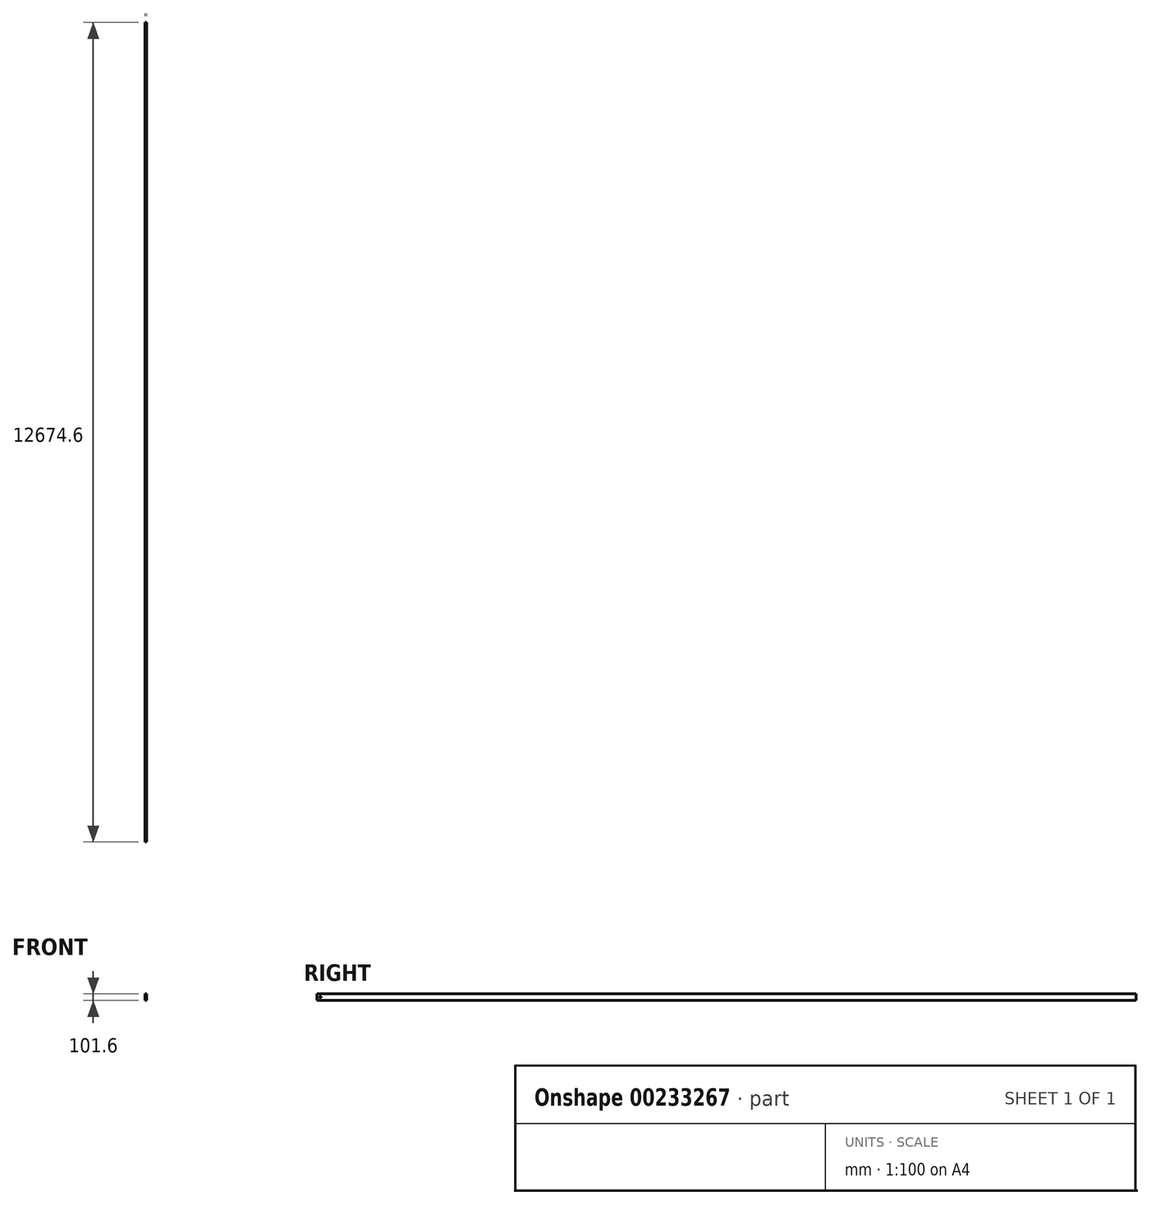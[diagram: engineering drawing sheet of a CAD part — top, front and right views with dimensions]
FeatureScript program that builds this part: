
annotation { "Feature Type Name" : "Feature", "Feature Type Description" : "" }
export const myFeature = defineFeature(function(context is Context, id is Id, definition is map)
    precondition{}
    {
        {
            var Q0;
            Q0=qCreatedBy(makeId("Front.planeOp"),FACE);
            var sketch = newSketch(context, id + "F0", { "sketchPlane" : qUnion([Q0])});
            skLineSegment(sketch, "E0.bottom", {"start": v(-208.2, 49.53) * mm, "end": v(12541.8, 49.53) * mm});
            skLineSegment(sketch, "E0.top", {"start": v(-208.2, -52.07) * mm, "end": v(12541.8, -52.07) * mm});
            skLineSegment(sketch, "E0.left", {"start": v(-208.2, 49.53) * mm, "end": v(-208.2, -52.07) * mm});
            skLineSegment(sketch, "E0.right", {"start": v(12541.8, 49.53) * mm, "end": v(12541.8, -52.07) * mm});
            skSolve(sketch);
        }
        {
            var Q0;
            Q0 = qSketchRegion(id + "F0", true);
            extrude(context, id + "F1", {"entities" : qUnion([Q0]), "depth" : 25.4 * mm});
        }
        {
            var Q0;
            Q0=makeQuery(id+"F1.opExtrude","SWEPT_BODY",BODY,{"disambiguationData":[OSD([sQuery(id+"F0.wireOp",EDGE,"E0.bottom"),sQuery(id+"F0.wireOp",EDGE,"E0.top"),sQuery(id+"F0.wireOp",EDGE,"E0.left"),sQuery(id+"F0.wireOp",EDGE,"E0.right")])]});
            deleteBodies(context, id + "F2", {"entities" : qUnion([Q0])});
        }
        {
            var Q0;
            Q0=qCreatedBy(makeId("Right.planeOp"),FACE);
            var sketch = newSketch(context, id + "F3", { "sketchPlane" : qUnion([Q0])});
            skLineSegment(sketch, "E1.bottom", {"start": v(-6457.05, -2757.95) * mm, "end": v(6217.55, -2757.95) * mm});
            skLineSegment(sketch, "E1.top", {"start": v(-6457.05, -2859.55) * mm, "end": v(6217.55, -2859.55) * mm});
            skLineSegment(sketch, "E1.left", {"start": v(-6457.05, -2757.95) * mm, "end": v(-6457.05, -2859.55) * mm});
            skLineSegment(sketch, "E1.right", {"start": v(6217.55, -2757.95) * mm, "end": v(6217.55, -2859.55) * mm});
            skCircle(sketch, "E2", {"center": v(-6406.25, -2808.75) * mm, "radius": 12.7 * mm});
            skSolve(sketch);
        }
        {
            var Q0;
            Q0 = qSketchRegion(id + "F3", true);
            extrude(context, id + "F4", {"entities" : qUnion([Q0]), "depth" : 25.4 * mm});
        }
        {
            var Q0;
            Q0 = qSketchRegion(id + "F3", true);
            extrude(context, id + "F5", {"entities" : qUnion([Q0]), "operationType" : NewBodyOperationType.ADD, "depth" : 25.4 * mm});
        }
    });
